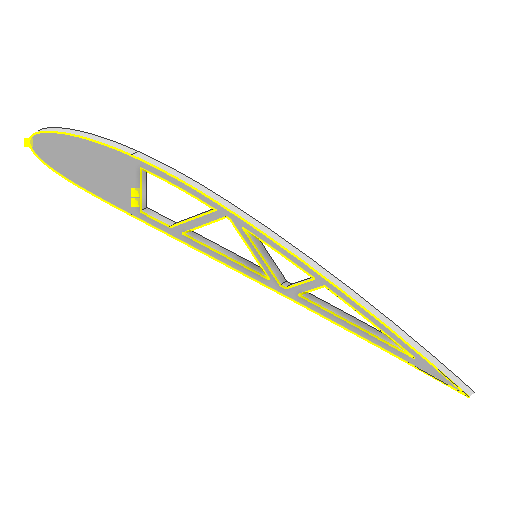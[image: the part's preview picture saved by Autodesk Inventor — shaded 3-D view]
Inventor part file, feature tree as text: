
AUTODESK INVENTOR PART (.ipt)
format: ipt  version: 2022 (Build 260153000, 153)  size: 287,232 bytes
history: native  units: mm
features: sketch x7, extrude x6, projected_geometry x4, shell x1
ambient origin geometry x8: Origin, YZ Plane, XZ Plane, XY Plane, X Axis, Y Axis, Z Axis, Center Point
bodies: Solid1 (feature_tree)
feature tree (18):
  extrude  "Extrusion1"  Depth=5.0mm
  shell  "Shell1"  Thickness=6.0mm
  extrude  "Extrusion2"  Depth=2.0mm
  extrude  "Extrusion3"  Depth=5.9mm
  extrude  "Extrusion4"  Depth=10.0mm TaperAngle=0.0deg
  extrude  "Extrusion5"  Depth=10.0mm TaperAngle=0.0deg
  extrude  "Extrusion7"  Depth=5.0mm
  sketch  "Sketch15"  dims[d20=5.0mm d22=4.5mm d23=0.0mm d24=2.0mm d26=2.0mm d29=4.5mm d30=0.0mm]
  sketch  "Sketch3"  dims[d0=4.5mm d1=0.0mm d2=5.0mm d3=6.0mm]
  sketch  "Sketch7"  dims[d5=4.5mm d6=0.0mm d7=2.0mm]
  projected_geometry  "Projected Loop3"
  sketch  "Sketch8"  dims[d8=2.0mm d9=5.9mm]
  sketch  "Sketch9"  dims[d12=4.0mm d13=10.0mm d14=0.0mm]
  sketch  "Sketch10"  dims[d15=70.0mm d16=10.0mm d17=0.0mm]
  projected_geometry  "Projected Loop4"
  sketch  "Sketch14"  dims[d18=5.0mm d19=5.0mm]
  projected_geometry  "Projected Loop7"
  projected_geometry  "Projected Loop8"
